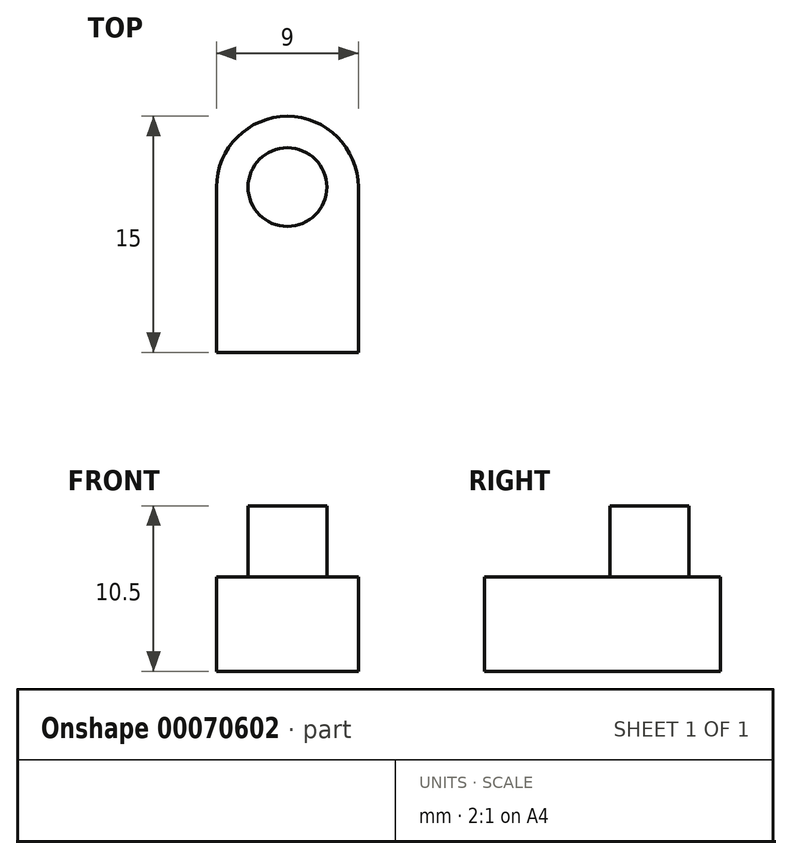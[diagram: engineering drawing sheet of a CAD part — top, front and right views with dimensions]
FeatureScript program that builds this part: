
annotation { "Feature Type Name" : "Feature", "Feature Type Description" : "" }
export const myFeature = defineFeature(function(context is Context, id is Id, definition is map)
    precondition{}
    {
        {
            var Q0;
            Q0=qCreatedBy(makeId("Top.planeOp"),FACE);
            var sketch = newSketch(context, id + "F0", { "sketchPlane" : qUnion([Q0])});
            skLineSegment(sketch, "E0.rect.bottom", {"start": v(-4.5, -7.5) * mm, "end": v(4.5, -7.5) * mm});
            skLineSegment(sketch, "E0.rect.top", {"start": v(-4.5, 7.5) * mm, "end": v(4.5, 7.5) * mm});
            skLineSegment(sketch, "E0.rect.left", {"start": v(-4.5, -7.5) * mm, "end": v(-4.5, 7.5) * mm});
            skLineSegment(sketch, "E0.rect.right", {"start": v(4.5, -7.5) * mm, "end": v(4.5, 7.5) * mm});
            skPoint(sketch, "E0.rect.middle", {"position": v(0, 0) * mm});
            skSolve(sketch);
        }
        {
            var Q0;
            Q0=makeQuery(id+"F0.imprint","IMPRINT",FACE,{"disambiguationData":[TD([[makeQuery(id+"F0.imprint","IMPRINT",EDGE,{"derivedFrom":sQuery(id+"F0.wireOp",EDGE,"E0.rect.bottom")}),1.0]])]});
            extrude(context, id + "F1", {"entities" : qUnion([Q0]), "depth" : 6 * mm});
        }
        {
            var Q0;
            Q0=makeQuery(id+"F1.opExtrude","CAP_FACE",FACE,{"disambiguationData":[OSD([sQuery(id+"F0.wireOp",EDGE,"E0.rect.bottom"),sQuery(id+"F0.wireOp",EDGE,"E0.rect.top"),sQuery(id+"F0.wireOp",EDGE,"E0.rect.left"),sQuery(id+"F0.wireOp",EDGE,"E0.rect.right")])],"isStart":false});
            var sketch = newSketch(context, id + "F2", { "sketchPlane" : qUnion([Q0])});
            skCircle(sketch, "E1", {"center": v(0, 3) * mm, "radius": 2.5 * mm});
            skSolve(sketch);
        }
        {
            var Q0;
            Q0=makeQuery(id+"F2.imprint","IMPRINT",FACE,{"disambiguationData":[TD([[makeQuery(id+"F2.imprint","IMPRINT",EDGE,{"derivedFrom":sQuery(id+"F2.wireOp",EDGE,"E1")}),1.0]])]});
            extrude(context, id + "F3", {"entities" : qUnion([Q0]), "operationType" : NewBodyOperationType.ADD, "depth" : 4.5 * mm});
        }
        {
            var Q0;
            Q0=makeQuery(id+"F1.opExtrude","SWEPT_EDGE",EDGE,{"disambiguationData":[OSD([sQuery(id+"F0.wireOp",EDGE,"E0.rect.top"),sQuery(id+"F0.wireOp",EDGE,"E0.rect.left")])]});
            var Q1;
            Q1=makeQuery(id+"F1.opExtrude","SWEPT_EDGE",EDGE,{"disambiguationData":[OSD([sQuery(id+"F0.wireOp",EDGE,"E0.rect.top"),sQuery(id+"F0.wireOp",EDGE,"E0.rect.right")])]});
            fillet(context, id + "F4", {"entities" : qUnion([Q0, Q1]), "radius" : 4.5 * mm, "tangentPropagation" : true, "allowEdgeOverflow" : false});
        }
    });
